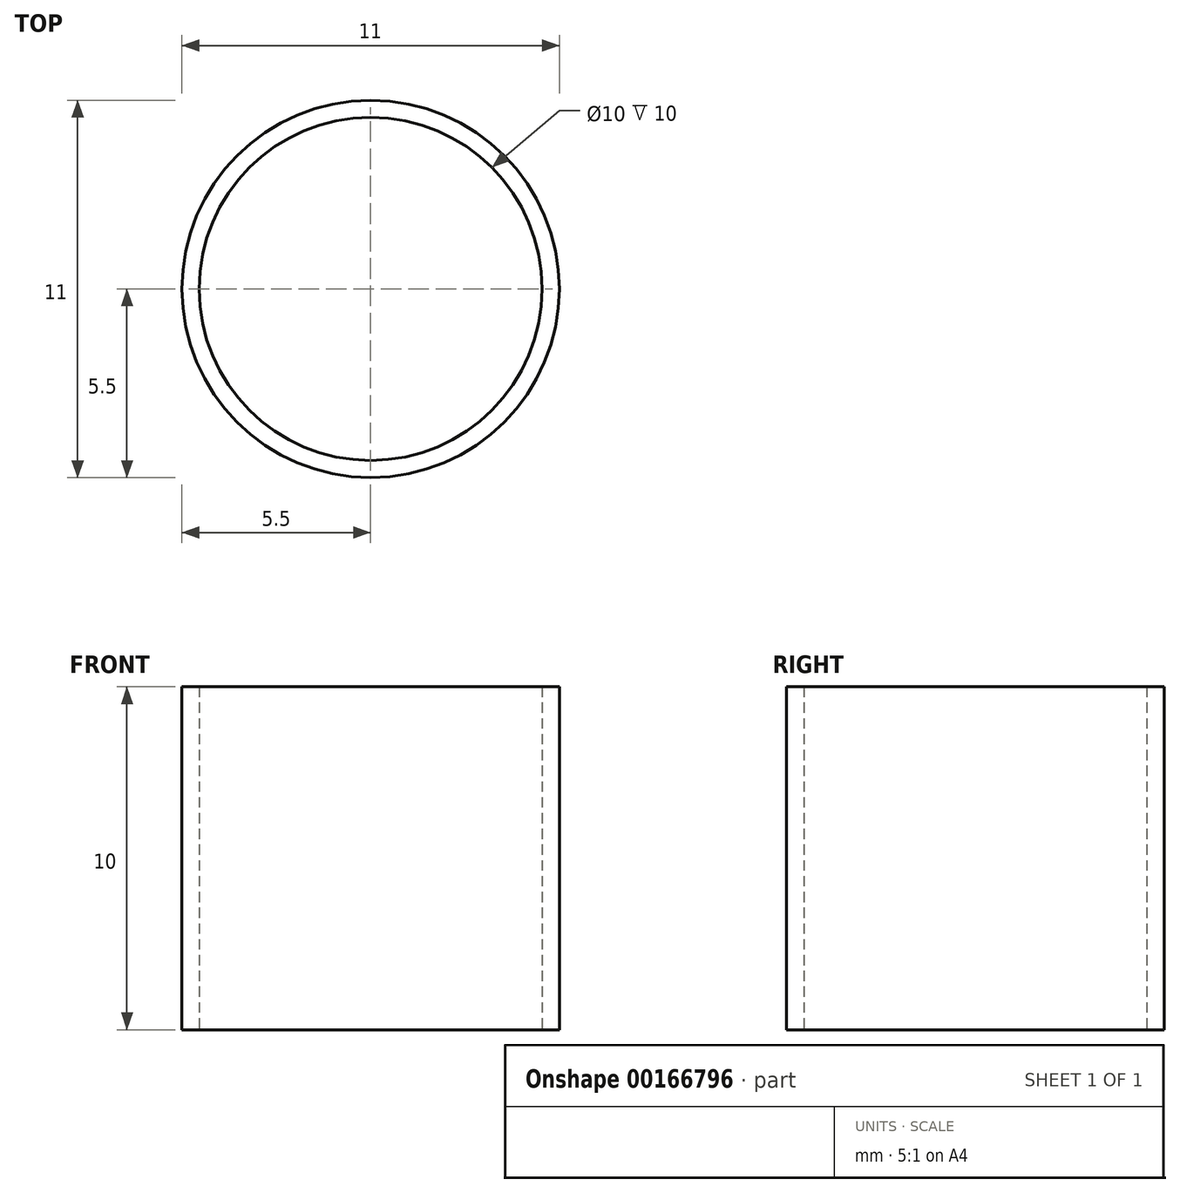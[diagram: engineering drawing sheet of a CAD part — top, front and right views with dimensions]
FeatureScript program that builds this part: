
annotation { "Feature Type Name" : "Feature", "Feature Type Description" : "" }
export const myFeature = defineFeature(function(context is Context, id is Id, definition is map)
    precondition{}
    {
        {
            var Q0;
            Q0=qCreatedBy(makeId("Top.planeOp"),FACE);
            var sketch = newSketch(context, id + "F0", { "sketchPlane" : qUnion([Q0])});
            skCircle(sketch, "E0", {"center": v(0, 0) * mm, "radius": 5.5 * mm});
            skCircle(sketch, "E1", {"center": v(0, 0) * mm, "radius": 5 * mm});
            skSolve(sketch);
        }
        {
            var Q0;
            Q0=makeQuery(id+"F0.imprint","IMPRINT",FACE,{"disambiguationData":[TD([[makeQuery(id+"F0.imprint","IMPRINT",EDGE,{"derivedFrom":sQuery(id+"F0.wireOp",EDGE,"E0")}),1.0]])]});
            extrude(context, id + "F1", {"entities" : qUnion([Q0]), "depth" : 10 * mm});
        }
    });
